# Revit family: Door-Access-Best Access Doors-Medium_Security_Surface_Mounted-BA-MSD
name_source: partatom
category: Specialty Equipment
revit_build: Autodesk Revit 2017 (Build: 20160225_1515(x64)
units: mm (PartAtom-declared; Revit-internal decimal feet)

## family parameters
Cut with Voids When Loaded = No
Host = Face
OmniClass Number = 23.30.10.27.17
Part Type = Normal
Room Calculation Point = No
Round Connector Dimension = Use Diameter
Shared = No

## types (8) — shared parameters
Assembly Code = C1020700
Construction Material = Metal - Best Access Doors - Aluminum
Default Elevation = 0"
Description = BA-MSD - Medium Security Access Door All Surface Types
Finish = Metal - Best Access Doors - Powder Coated White
Frame Depth = 1 7/16"
Manufacturer = Best Access Doors
Model = BA-MSD
Product data url = https://bimobject.com
URL = https://www.bestaccessdoors.com

## per-type parameters (varying)
| type | Door Height | Door Width | Height Actual | Height Calc | Width Actual | Width Calc |
| Custom | 24" | 24" | 26" | 24" | 26" | 24" |
| 12 x 12 | 12" | 12" | 14" | 12" | 14" | 12" |
| 16 x 16 | 16" | 16" | 18" | 16" | 18" | 16" |
| 18 x 18 | 18" | 18" | 20" | 18" | 20" | 18" |
| 24 x 24 | 24" | 24" | 26" | 24" | 26" | 24" |
| 24 x 30 | 30" | 24" | 32" | 30" | 26" | 24" |
| 24 x 36 | 36" | 24" | 38" | 36" | 26" | 24" |
| 36 x 36 | 36" | 36" | 38" | 36" | 38" | 36" |

## geometry (parser evidence)
native form markers: Blend x4, Sweep x15
no freeform markers — native parametric forms only
